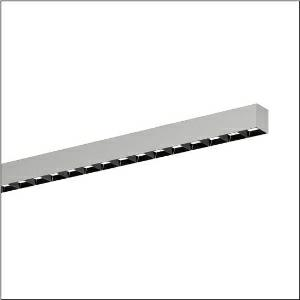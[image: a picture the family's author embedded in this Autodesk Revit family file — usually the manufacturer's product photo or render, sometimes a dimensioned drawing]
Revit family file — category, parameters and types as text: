
# Revit family: silica_r__21_51mx22dc4asb_d7c9
name_source: partatom
category: Lighting Fixtures
units: mm (PartAtom-declared; Revit-internal decimal feet)

## family parameters
Cut with Voids When Loaded = No
Host = Face
Light Source = No
Part Type = Normal
Room Calculation Point = No
Round Connector Dimension = Use Diameter
Shared = No

## types (1)
- --- (1 x LED, 10800 lm, 64.7 W, 4000K)
    Apparent Load = 65 VA
    CIE Flux Codes = 86 100 100 100 100
    Color Rendering = 80
    Color Temperature = 4000K
    Default Elevation = 1800 mm
    Description = Silica® 21, office luminaire, primary light control with darklight reflector, of PMMA, black, CAT 2 (L<= 3000cd/m²), light emission: direct distribution, primary light characteristic: symmetric, installation type: surface-mounted, LED, rated luminous flux: 10.800lm, luminous efficacy: 167lm/W, light colour: 840, colour temperature: 4000K, control gear: DALI 2, with terminal, 3+2-pole, max. 2.5mm², mains connection: 220..240V, AC, 50/60Hz, rated input power: 64.7W, luminaire housing, of aluminium, metallic grey (RAL 9006), length: 3.004mm, width: 53mm, height: 53mm, protection rating (complete): IP20, insulation class (complete): insulation class I (protective earthing), certification: CE, permissible operating ambient temperature: 0..+35°C, standard: EN 50419, packaging unit: 1 piece
    Height = 53 mm
    Lamp = 1 x LED
    Lamp Light Flux = 10800 lm
    Lamp Power = 64.7 W
    Lamp count = 1
    Length = 3004 mm
    Luminous efficacy = 167 lm/W
    Manufacturer = Siteco
    ModVariant = No
    Model = 51MX22DC4ASB
    Mounting Place = Ceiling
    Mounting Type = Surface mounted
    Number of Poles = 1
    OnlyDefault = Yes
    Power Factor = 1
    Product Name = Silica® 21
    Product group = office luminaire | ceiling mounted
    ProductGroupID = 302
    Protection Class = Protection class I
    Protection Degree = IP 20
    RLX_Detail_Level = 1
    RLX_Emergency_Light_Flux = 0 lm
    RLX_Emergency_Type = 0
    RLX_Emergency_Type_DB = No
    RlxData = <blob elided: 63685 chars, md5=99ea719c>
    Socket = socket
    Standby Power = 0 W
    System Light Flux = 10800 lm
    System Power = 65 W
    Type Comments = factory setting: luminous flux: 100 % | dim-lin: 254 | 366 mA
    Type Image = l_1335929.jpg
    URL = http://relux.com
    VarID = @adj_124546
    Voltage = 0 V
    Weight = 0.00 kg
    Width = 53 mm

## geometry (parser evidence)
native form markers: Blend x4, Sweep x9
no freeform markers — native parametric forms only
